AUTODESK INVENTOR PART (.ipt)
format: ipt  version: 2012 (Build 160160000, 160)  size: 731,648 bytes
history: native  units: mm (DEFAULTED — no unit token found)
features: plane x3, other x3, sketch x2, extrude x1
ambient origin geometry x8: Origin, YZ Plane, XZ Plane, XY Plane, X Axis, Y Axis, Z Axis, Center Point
bodies: Solid1 (feature_tree)
feature tree (9):
  extrude  "Extrusion1"  Depth=7.5mm TaperAngle=0.0deg
  plane  "Work Plane2"
  plane  "Work Plane8"
  plane  "Work Plane9"
  other  "Spur Gear"
  sketch  "Sketch1"  dims[d0=44.408304mm d1=7.5mm d2=0.0mm]
  sketch  "Sketch2"  dims[d3=44.1mm d4=10.0mm d5=0.0mm d16=44.1mm d17=0.0mm d34=0.668424mm d39=0.0mm d41=0.0mm d43=44.1mm d46=44.1mm d47=0.0mm d48=0.0mm]
  other  "Srf1"
  other  "Pitch Diameter"
